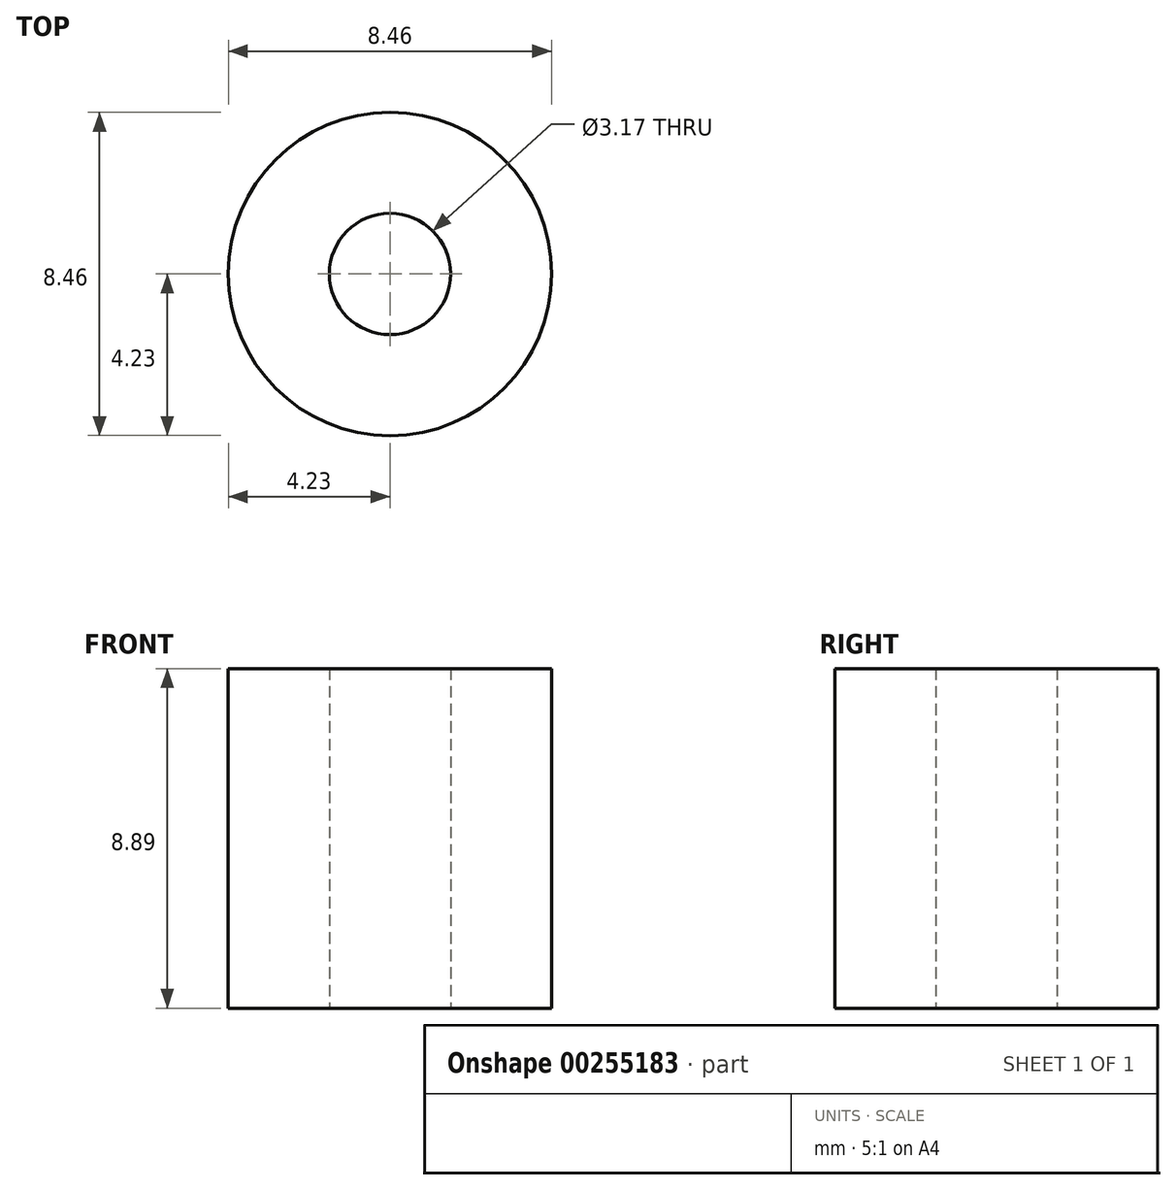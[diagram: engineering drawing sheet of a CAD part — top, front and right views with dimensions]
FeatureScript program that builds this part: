
annotation { "Feature Type Name" : "Feature", "Feature Type Description" : "" }
export const myFeature = defineFeature(function(context is Context, id is Id, definition is map)
    precondition{}
    {
        {
            var Q0;
            Q0=qCreatedBy(makeId("Top.planeOp"),FACE);
            var sketch = newSketch(context, id + "F0", { "sketchPlane" : qUnion([Q0])});
            skCircle(sketch, "E0", {"center": v(0, 0) * mm, "radius": 1.59 * mm});
            skCircle(sketch, "E1", {"center": v(0, 0) * mm, "radius": 4.23 * mm});
            skSolve(sketch);
        }
        {
            var Q0;
            Q0 = qSketchRegion(id + "F0", true);
            extrude(context, id + "F1", {"entities" : qUnion([Q0]), "depth" : 8.9 * mm});
        }
    });
